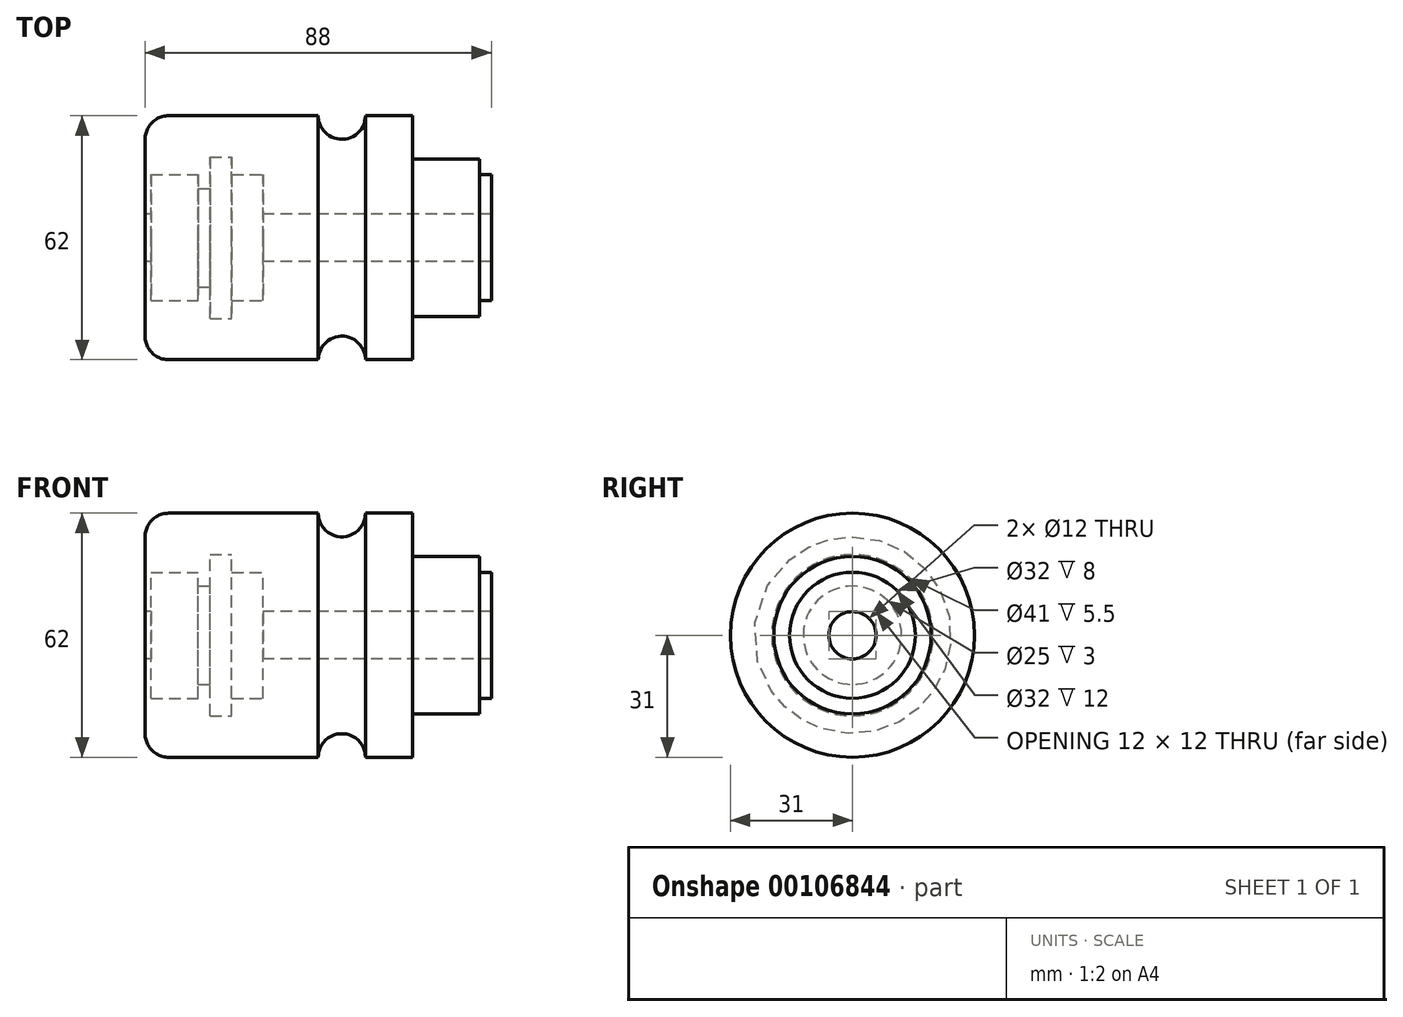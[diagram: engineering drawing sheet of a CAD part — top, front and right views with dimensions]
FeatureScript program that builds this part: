
annotation { "Feature Type Name" : "Feature", "Feature Type Description" : "" }
export const myFeature = defineFeature(function(context is Context, id is Id, definition is map)
    precondition{}
    {
        {
            var Q0;
            Q0=qCreatedBy(makeId("Front.planeOp"),FACE);
            var sketch = newSketch(context, id + "F0", { "sketchPlane" : qUnion([Q0])});
            skLineSegment(sketch, "E0", {"start": v(-23.4, 0) * mm, "end": v(22.85, 0) * mm, "construction": true});
            skLineSegment(sketch, "E1.bottom", {"start": v(0, 6) * mm, "end": v(3, 6) * mm});
            skLineSegment(sketch, "E1.top", {"start": v(0, 16) * mm, "end": v(3, 16) * mm});
            skLineSegment(sketch, "E1.left", {"start": v(0, 6) * mm, "end": v(0, 16) * mm});
            skLineSegment(sketch, "E1.right", {"start": v(3, 6) * mm, "end": v(3, 16) * mm});
            skLineSegment(sketch, "E2.bottom", {"start": v(0, 6) * mm, "end": v(-17, 6) * mm});
            skLineSegment(sketch, "E2.top", {"start": v(0, 20) * mm, "end": v(-17, 20) * mm});
            skLineSegment(sketch, "E2.left", {"start": v(0, 6) * mm, "end": v(0, 20) * mm});
            skLineSegment(sketch, "E2.right", {"start": v(-17, 6) * mm, "end": v(-17, 20) * mm});
            skLineSegment(sketch, "E3.bottom", {"start": v(-17, 6) * mm, "end": v(-29, 6) * mm});
            skLineSegment(sketch, "E3.top", {"start": v(-17, 31) * mm, "end": v(-29, 31) * mm});
            skLineSegment(sketch, "E3.left", {"start": v(-17, 6) * mm, "end": v(-17, 31) * mm});
            skLineSegment(sketch, "E3.right", {"start": v(-29, 6) * mm, "end": v(-29, 31) * mm});
            skLineSegment(sketch, "E4.bottom", {"start": v(-41, 6) * mm, "end": v(-85, 6) * mm});
            skLineSegment(sketch, "E4.top", {"start": v(-41, 31) * mm, "end": v(-85, 31) * mm});
            skLineSegment(sketch, "E4.left", {"start": v(-41, 6) * mm, "end": v(-41, 31) * mm});
            skLineSegment(sketch, "E4.right", {"start": v(-85, 6) * mm, "end": v(-85, 31) * mm});
            skArc(sketch, "E5", {"start": v(-41, 31) * mm, "mid": v(-35, 25) * mm, "end": v(-29, 31) * mm});
            skLineSegment(sketch, "E6", {"start": v(-41, 6) * mm, "end": v(-29, 6) * mm});
            skSolve(sketch);
        }
        {
            var Q0;
            Q0 = qSketchRegion(id + "F0", true);
            var Q1;
            Q1=sQuery(id+"F0.wireOp",EDGE,"E0");
            revolve(context, id + "F1", {"entities" : qUnion([Q0]), "axis" : qUnion([Q1]), "revolveType" : RevolveType.FULL});
        }
        {
            var Q0;
            Q0=makeQuery(id+"F1.opRevolve","SWEPT_EDGE",EDGE,{"disambiguationData":[OSD([sQuery(id+"F0.wireOp",EDGE,"E4.top"),sQuery(id+"F0.wireOp",EDGE,"E4.right")])]});
            fillet(context, id + "F2", {"entities" : qUnion([Q0]), "radius" : 6 * mm, "tangentPropagation" : true, "allowEdgeOverflow" : false});
        }
        {
            var Q0;
            Q0=qCreatedBy(makeId("Front.planeOp"),FACE);
            var sketch = newSketch(context, id + "F3", { "sketchPlane" : qUnion([Q0])});
            skLineSegment(sketch, "E7", {"start": v(-47.69, 0) * mm, "end": v(-30.19, 0) * mm, "construction": true});
            skLineSegment(sketch, "E8", {"start": v(-83.5, 16) * mm, "end": v(-83.5, -46) * mm});
            skLineSegment(sketch, "E9.bottom", {"start": v(-83.5, 16) * mm, "end": v(-71.5, 16) * mm});
            skLineSegment(sketch, "E9.top", {"start": v(-83.5, 6) * mm, "end": v(-71.5, 6) * mm});
            skLineSegment(sketch, "E9.left", {"start": v(-83.5, 16) * mm, "end": v(-83.5, 6) * mm});
            skLineSegment(sketch, "E9.right", {"start": v(-71.5, 16) * mm, "end": v(-71.5, 6) * mm});
            skLineSegment(sketch, "E10.bottom", {"start": v(-71.5, 12.5) * mm, "end": v(-68.5, 12.5) * mm});
            skLineSegment(sketch, "E10.top", {"start": v(-71.5, 6) * mm, "end": v(-68.5, 6) * mm});
            skLineSegment(sketch, "E10.left", {"start": v(-71.5, 12.5) * mm, "end": v(-71.5, 6) * mm});
            skLineSegment(sketch, "E10.right", {"start": v(-68.5, 12.5) * mm, "end": v(-68.5, 6) * mm});
            skLineSegment(sketch, "E11.bottom", {"start": v(-68.5, 6) * mm, "end": v(-63, 6) * mm});
            skLineSegment(sketch, "E11.top", {"start": v(-68.5, 20.5) * mm, "end": v(-63, 20.5) * mm});
            skLineSegment(sketch, "E11.left", {"start": v(-68.5, 6) * mm, "end": v(-68.5, 20.5) * mm});
            skLineSegment(sketch, "E11.right", {"start": v(-63, 6) * mm, "end": v(-63, 20.5) * mm});
            skLineSegment(sketch, "E12.bottom", {"start": v(-63, 16) * mm, "end": v(-55, 16) * mm});
            skLineSegment(sketch, "E12.top", {"start": v(-63, 6) * mm, "end": v(-55, 6) * mm});
            skLineSegment(sketch, "E12.left", {"start": v(-63, 16) * mm, "end": v(-63, 6) * mm});
            skLineSegment(sketch, "E12.right", {"start": v(-55, 16) * mm, "end": v(-55, 6) * mm});
            skSolve(sketch);
        }
        {
            var Q0;
            Q0 = qSketchRegion(id + "F3", true);
            var Q1;
            Q1=sQuery(id+"F3.wireOp",EDGE,"E7");
            revolve(context, id + "F4", {"operationType" : NewBodyOperationType.REMOVE, "entities" : qUnion([Q0]), "axis" : qUnion([Q1]), "revolveType" : RevolveType.FULL, "oppositeDirection" : true});
        }
    });
